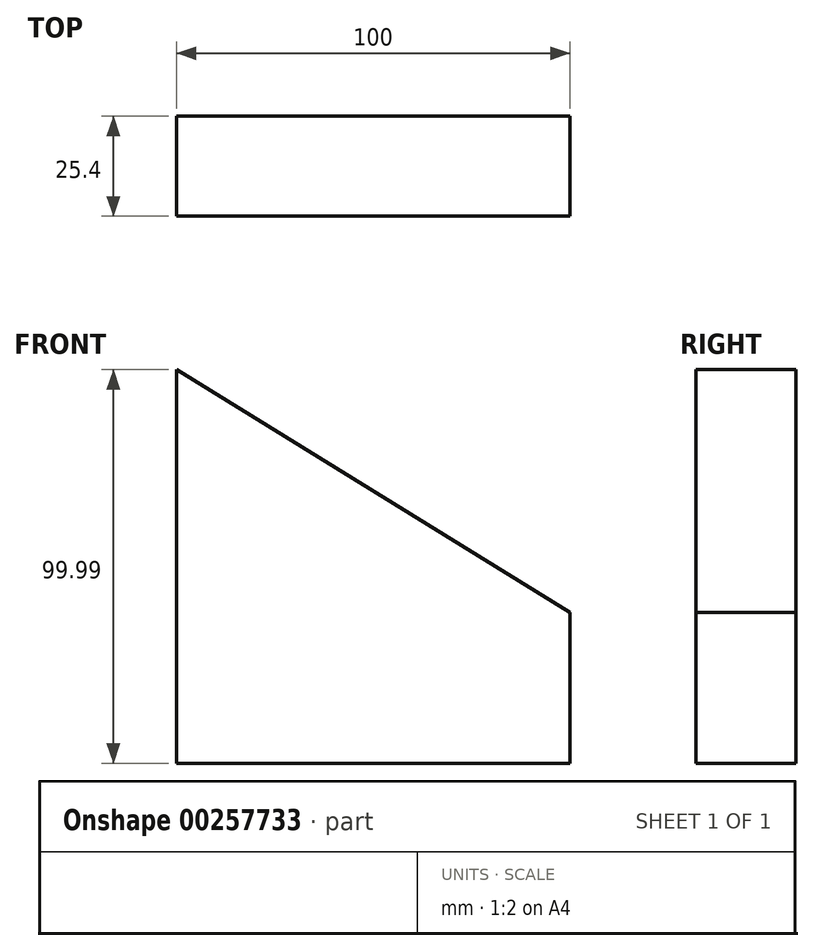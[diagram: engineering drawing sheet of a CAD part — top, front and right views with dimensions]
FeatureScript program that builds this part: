
annotation { "Feature Type Name" : "Feature", "Feature Type Description" : "" }
export const myFeature = defineFeature(function(context is Context, id is Id, definition is map)
    precondition{}
    {
        {
            var Q0;
            Q0=qCreatedBy(makeId("Front.planeOp"),FACE);
            var sketch = newSketch(context, id + "F0", { "sketchPlane" : qUnion([Q0])});
            skLineSegment(sketch, "E0", {"start": v(0, 0) * mm, "end": v(-100, 0) * mm});
            skLineSegment(sketch, "E1", {"start": v(-100, 0) * mm, "end": v(-100, 99.99) * mm});
            skLineSegment(sketch, "E2", {"start": v(-100, 99.99) * mm, "end": v(0, 38.27) * mm});
            skLineSegment(sketch, "E3", {"start": v(0, 38.27) * mm, "end": v(0, 0) * mm});
            skSolve(sketch);
        }
        {
            var Q0;
            Q0=makeQuery(id+"F0.imprint","IMPRINT",FACE,{"disambiguationData":[TD([[makeQuery(id+"F0.imprint","IMPRINT",EDGE,{"derivedFrom":sQuery(id+"F0.wireOp",EDGE,"E0")}),-1.0]])]});
            extrude(context, id + "F1", {"entities" : qUnion([Q0]), "depth" : 25.4 * mm});
        }
    });
